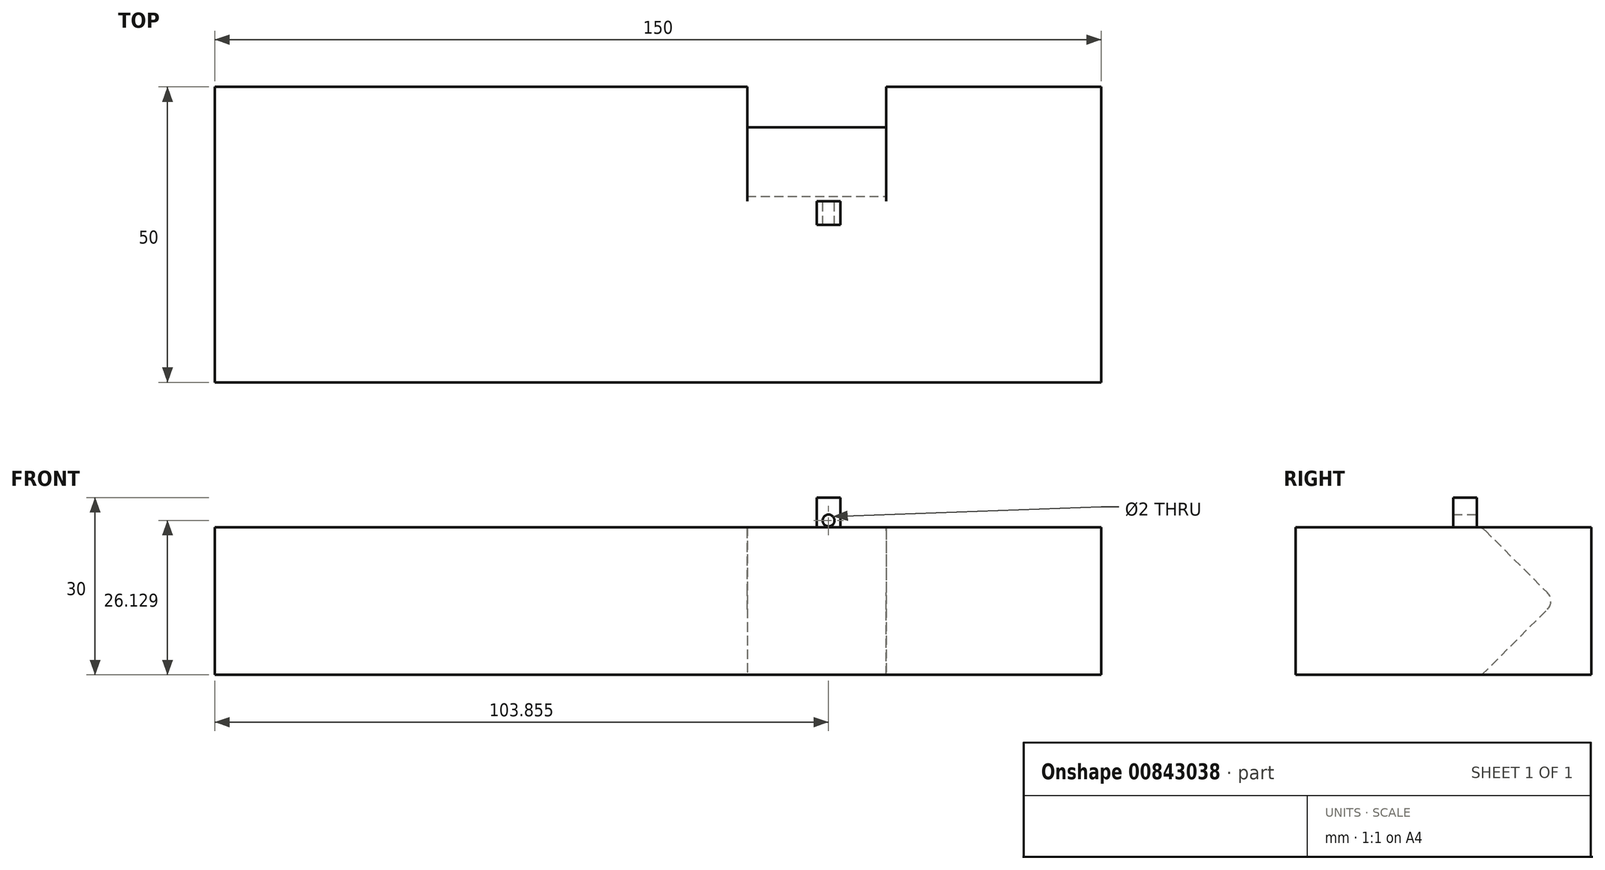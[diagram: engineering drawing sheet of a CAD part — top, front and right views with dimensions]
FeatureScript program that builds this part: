
annotation { "Feature Type Name" : "Feature", "Feature Type Description" : "" }
export const myFeature = defineFeature(function(context is Context, id is Id, definition is map)
    precondition{}
    {
        {
            var Q0;
            Q0=qCreatedBy(makeId("Top.planeOp"),FACE);
            var sketch = newSketch(context, id + "F0", { "sketchPlane" : qUnion([Q0])});
            skLineSegment(sketch, "E0.bottom", {"start": v(-74.89, 16.13) * mm, "end": v(15.2, 16.13) * mm});
            skLineSegment(sketch, "E0.top", {"start": v(-74.89, -33.87) * mm, "end": v(75.11, -33.87) * mm});
            skLineSegment(sketch, "E0.left", {"start": v(-74.89, 16.13) * mm, "end": v(-74.89, -33.87) * mm});
            skLineSegment(sketch, "E0.right", {"start": v(75.11, 16.13) * mm, "end": v(75.11, -33.87) * mm});
            skLineSegment(sketch, "E1", {"start": v(15.2, 16.13) * mm, "end": v(15.2, 10.13) * mm});
            skLineSegment(sketch, "E2", {"start": v(15.2, 10.13) * mm, "end": v(38.72, 10.13) * mm});
            skLineSegment(sketch, "E3", {"start": v(38.72, 16.13) * mm, "end": v(38.72, 10.13) * mm});
            skLineSegment(sketch, "E4.trimOffspring", {"start": v(38.72, 16.13) * mm, "end": v(75.11, 16.13) * mm});
            skSolve(sketch);
        }
        {
            var Q0;
            Q0=makeQuery(id+"F0.imprint","IMPRINT",FACE,{"disambiguationData":[TD([[makeQuery(id+"F0.imprint","IMPRINT",EDGE,{"derivedFrom":sQuery(id+"F0.wireOp",EDGE,"E0.bottom")}),-1.0]])]});
            extrude(context, id + "F1", {"entities" : qUnion([Q0]), "depth" : 25 * mm, "offsetDistance" : 25 * mm});
        }
        {
            var Q0;
            Q0=makeQuery(id+"F1.opExtrude","SWEPT_FACE",FACE,{"disambiguationData":[OSD([sQuery(id+"F0.wireOp",EDGE,"E2")])]});
            var sketch = newSketch(context, id + "F2", { "sketchPlane" : qUnion([Q0])});
            skLineSegment(sketch, "E5", {"start": v(-38.72, 12.5) * mm, "end": v(-15.2, 12.5) * mm});
            skLineSegment(sketch, "E6", {"start": v(-38.72, 12.5) * mm, "end": v(-38.72, 25) * mm});
            skLineSegment(sketch, "E7", {"start": v(-38.72, 25) * mm, "end": v(-15.2, 25) * mm});
            skLineSegment(sketch, "E8", {"start": v(-15.2, 25) * mm, "end": v(-15.2, 12.5) * mm});
            skCircle(sketch, "E9", {"center": v(-26.97, 17.72) * mm, "radius": 1.25 * mm});
            skPoint(sketch, "E9.centerSnap0", {"position": v(-26.97, 12.5) * mm});
            skSolve(sketch);
        }
        {
            var Q0;
            Q0=makeQuery(id+"F1.opExtrude","CAP_EDGE",EDGE,{"disambiguationData":[OSD([sQuery(id+"F0.wireOp",EDGE,"E2")])],"isStart":false});
            var Q1;
            Q1=makeQuery(id+"F1.opExtrude","CAP_EDGE",EDGE,{"disambiguationData":[OSD([sQuery(id+"F0.wireOp",EDGE,"E2")])],"isStart":true});
            chamfer(context, id + "F3", {"entities" : qUnion([Q0, Q1]), "width" : 12.5 * mm, "tangentPropagation" : true});
        }
        {
            var Q0;
            {var subQ0=sQuery(id+"F0.wireOp",EDGE,"E2");Q0=makeQuery(id+"F3.opChamfer","BLEND_EDGE",EDGE,{"blendedFrom":[makeQuery(id+"F1.opExtrude","CAP_EDGE",EDGE,{"disambiguationData":[OSD([subQ0])],"isStart":true}),makeQuery(id+"F1.opExtrude","CAP_EDGE",EDGE,{"disambiguationData":[OSD([subQ0])],"isStart":false})],"blendedInto":[]});}
            fillet(context, id + "F4", {"entities" : qUnion([Q0]), "radius" : 2 * mm, "tangentPropagation" : true, "allowEdgeOverflow" : false});
        }
        {
            var Q0;
            {var subQ0=sQuery(id+"F0.wireOp",EDGE,"E2");Q0=makeQuery(id+"F3.opChamfer","BLEND_EDGE",EDGE,{"blendedFrom":[makeQuery(id+"F1.opExtrude","CAP_EDGE",EDGE,{"disambiguationData":[OSD([subQ0])],"isStart":false}),makeQuery(id+"F1.opExtrude","CAP_FACE",FACE,{"disambiguationData":[OSD([sQuery(id+"F0.wireOp",EDGE,"E0.bottom"),sQuery(id+"F0.wireOp",EDGE,"E0.top"),sQuery(id+"F0.wireOp",EDGE,"E0.left"),sQuery(id+"F0.wireOp",EDGE,"E0.right"),sQuery(id+"F0.wireOp",EDGE,"E1"),subQ0,sQuery(id+"F0.wireOp",EDGE,"E3"),sQuery(id+"F0.wireOp",EDGE,"E4.trimOffspring")])],"isStart":false})],"blendedInto":[makeQuery(id+"F1.opExtrude","CAP_FACE",FACE,{"disambiguationData":[OSD([sQuery(id+"F0.wireOp",EDGE,"E0.bottom"),sQuery(id+"F0.wireOp",EDGE,"E0.top"),sQuery(id+"F0.wireOp",EDGE,"E0.left"),sQuery(id+"F0.wireOp",EDGE,"E0.right"),sQuery(id+"F0.wireOp",EDGE,"E1"),subQ0,sQuery(id+"F0.wireOp",EDGE,"E3"),sQuery(id+"F0.wireOp",EDGE,"E4.trimOffspring")])],"isStart":false})]});}
            fillet(context, id + "F5", {"entities" : qUnion([Q0]), "radius" : 2 * mm, "tangentPropagation" : true, "allowEdgeOverflow" : false});
        }
        {
            var Q0;
            Q0=makeQuery(id+"F1.opExtrude","CAP_FACE",FACE,{"disambiguationData":[OSD([sQuery(id+"F0.wireOp",EDGE,"E0.bottom"),sQuery(id+"F0.wireOp",EDGE,"E0.top"),sQuery(id+"F0.wireOp",EDGE,"E0.left"),sQuery(id+"F0.wireOp",EDGE,"E0.right"),sQuery(id+"F0.wireOp",EDGE,"E1"),sQuery(id+"F0.wireOp",EDGE,"E2"),sQuery(id+"F0.wireOp",EDGE,"E3"),sQuery(id+"F0.wireOp",EDGE,"E4.trimOffspring")])],"isStart":false});
            var sketch = newSketch(context, id + "F6", { "sketchPlane" : qUnion([Q0])});
            skLineSegment(sketch, "E10.bottom", {"start": v(26.97, -3.2) * mm, "end": v(30.97, -3.2) * mm});
            skLineSegment(sketch, "E10.top", {"start": v(26.97, -7.2) * mm, "end": v(30.97, -7.2) * mm});
            skLineSegment(sketch, "E10.left", {"start": v(26.97, -3.2) * mm, "end": v(26.97, -7.2) * mm});
            skLineSegment(sketch, "E10.right", {"start": v(30.97, -3.2) * mm, "end": v(30.97, -7.2) * mm});
            skSolve(sketch);
        }
        {
            var Q0;
            Q0=makeQuery(id+"F6.imprint","IMPRINT",FACE,{"disambiguationData":[TD([[makeQuery(id+"F6.imprint","IMPRINT",EDGE,{"derivedFrom":sQuery(id+"F6.wireOp",EDGE,"E10.bottom")}),1.0]])]});
            extrude(context, id + "F7", {"entities" : qUnion([Q0]), "operationType" : NewBodyOperationType.ADD, "depth" : 5 * mm, "offsetDistance" : 25 * mm});
        }
        {
            var Q0;
            Q0=makeQuery(id+"F7.opExtrude","SWEPT_FACE",FACE,{"disambiguationData":[OSD([sQuery(id+"F6.wireOp",EDGE,"E10.bottom")])]});
            var sketch = newSketch(context, id + "F8", { "sketchPlane" : qUnion([Q0])});
            skPoint(sketch, "E11.centerSnap0", {"position": v(-26.97, 27.5) * mm});
            skPoint(sketch, "E11.centerSnap1", {"position": v(-28.97, 25) * mm});
            skLineSegment(sketch, "E12", {"start": v(-28.97, 27.5) * mm, "end": v(-28.97, 26.13) * mm, "construction": true});
            skSolve(sketch);
        }
        {
            var Q0;
            Q0=sQuery(id+"F8.wireOp",VERTEX,"E12.end");
            var Q1;
            Q1=makeQuery(id+"F1.opExtrude","SWEPT_BODY",BODY,{"disambiguationData":[OSD([sQuery(id+"F0.wireOp",EDGE,"E0.bottom"),sQuery(id+"F0.wireOp",EDGE,"E0.top"),sQuery(id+"F0.wireOp",EDGE,"E0.left"),sQuery(id+"F0.wireOp",EDGE,"E0.right"),sQuery(id+"F0.wireOp",EDGE,"E1"),sQuery(id+"F0.wireOp",EDGE,"E2"),sQuery(id+"F0.wireOp",EDGE,"E3"),sQuery(id+"F0.wireOp",EDGE,"E4.trimOffspring")])]});
            hole(context, id + "F9", {"style" : HoleStyle.SIMPLE, "endStyle" : HoleEndStyle.THROUGH, "holeDiameter" : 2 * mm, "majorDiameter" : 5 * mm, "isTappedThrough" : true, "tappedDepth" : 12 * mm, "tapClearance" : 3, "locations" : qUnion([Q0]), "scope" : qUnion([Q1])});
        }
    });
